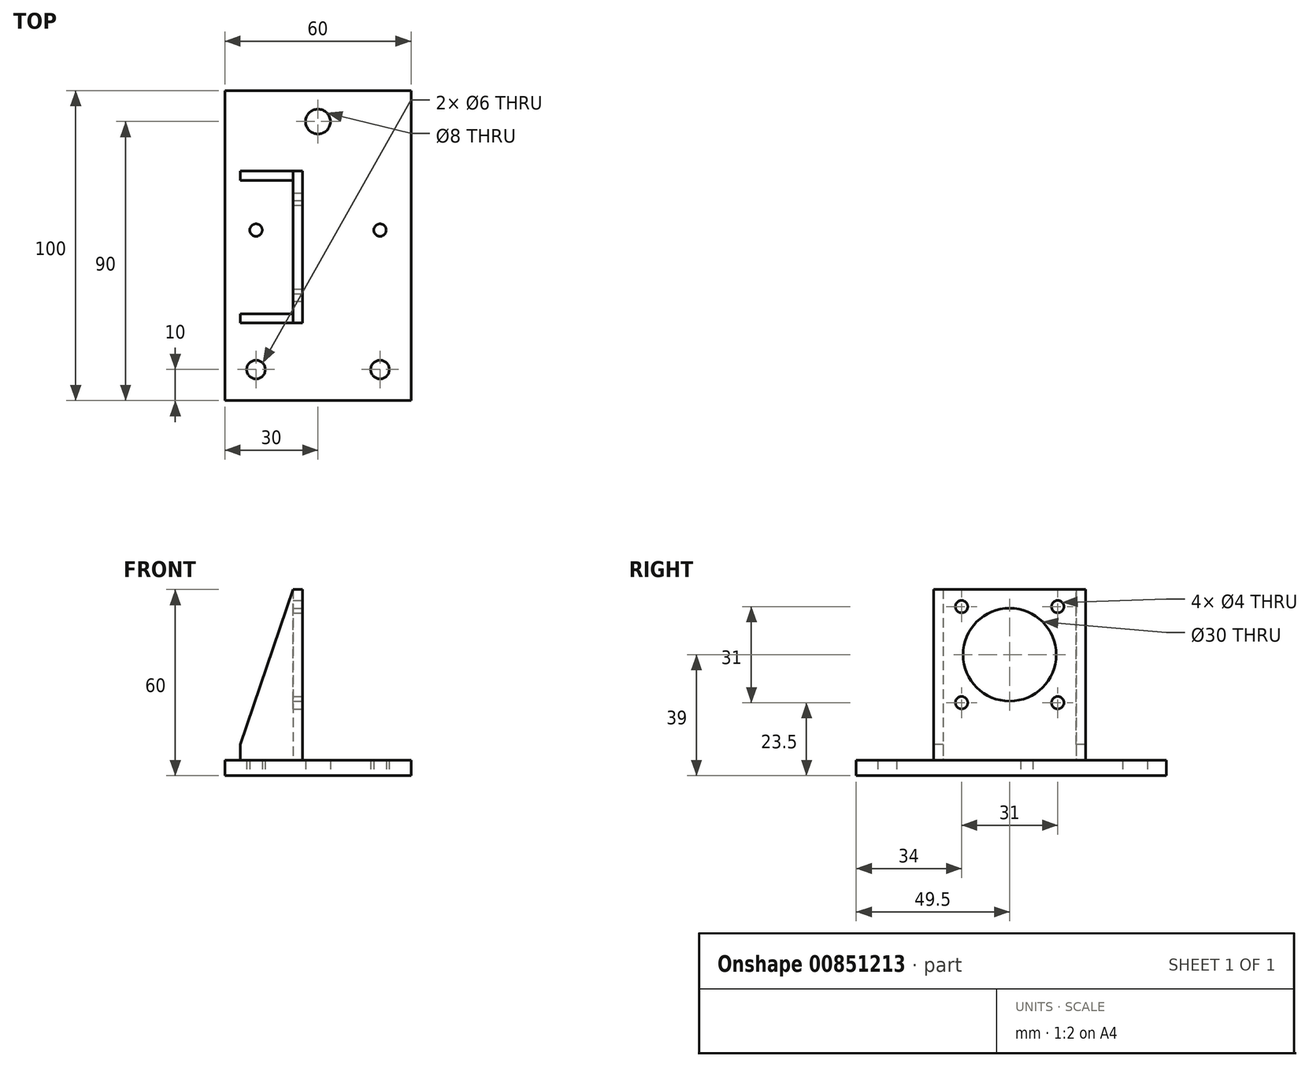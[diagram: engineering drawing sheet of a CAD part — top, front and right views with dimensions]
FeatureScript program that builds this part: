
annotation { "Feature Type Name" : "Feature", "Feature Type Description" : "" }
export const myFeature = defineFeature(function(context is Context, id is Id, definition is map)
    precondition{}
    {
        {
            var Q0;
            Q0=qCreatedBy(makeId("Top.planeOp"),FACE);
            var sketch = newSketch(context, id + "F0", { "sketchPlane" : qUnion([Q0])});
            skLineSegment(sketch, "E0.bottom", {"start": v(0, 0) * mm, "end": v(60, 0) * mm});
            skLineSegment(sketch, "E0.top", {"start": v(0, 100) * mm, "end": v(60, 100) * mm});
            skLineSegment(sketch, "E0.left", {"start": v(0, 0) * mm, "end": v(0, 100) * mm});
            skLineSegment(sketch, "E0.right", {"start": v(60, 0) * mm, "end": v(60, 100) * mm});
            skCircle(sketch, "E1", {"center": v(30, 90) * mm, "radius": 4 * mm});
            skPoint(sketch, "E1.centerSnap0", {"position": v(30, 100) * mm});
            skCircle(sketch, "E2", {"center": v(10, 10) * mm, "radius": 3 * mm});
            skCircle(sketch, "E3", {"center": v(50, 10) * mm, "radius": 3 * mm});
            skCircle(sketch, "E4", {"center": v(10, 55) * mm, "radius": 2 * mm});
            skCircle(sketch, "E5", {"center": v(50, 55) * mm, "radius": 2 * mm});
            skSolve(sketch);
        }
        {
            var Q0;
            Q0 = qSketchRegion(id + "F0", true);
            extrude(context, id + "F1", {"entities" : qUnion([Q0]), "depth" : 5 * mm, "offsetDistance" : 25 * mm});
        }
        {
            var Q0;
            Q0=makeQuery(id+"F1.opExtrude","CAP_FACE",FACE,{"disambiguationData":[OSD([sQuery(id+"F0.wireOp",EDGE,"E0.bottom"),sQuery(id+"F0.wireOp",EDGE,"E0.top"),sQuery(id+"F0.wireOp",EDGE,"E0.left"),sQuery(id+"F0.wireOp",EDGE,"E0.right"),sQuery(id+"F0.wireOp",EDGE,"E1"),sQuery(id+"F0.wireOp",EDGE,"E2"),sQuery(id+"F0.wireOp",EDGE,"E3"),sQuery(id+"F0.wireOp",EDGE,"E4"),sQuery(id+"F0.wireOp",EDGE,"E5")])],"isStart":false});
            var sketch = newSketch(context, id + "F2", { "sketchPlane" : qUnion([Q0])});
            skLineSegment(sketch, "E6", {"start": v(5, 74) * mm, "end": v(5, 71) * mm});
            skLineSegment(sketch, "E7", {"start": v(5, 71) * mm, "end": v(22, 71) * mm});
            skLineSegment(sketch, "E8", {"start": v(22, 71) * mm, "end": v(22, 28) * mm});
            skLineSegment(sketch, "E9", {"start": v(22, 28) * mm, "end": v(5, 28) * mm});
            skLineSegment(sketch, "E10", {"start": v(5, 28) * mm, "end": v(5, 25) * mm});
            skLineSegment(sketch, "E11", {"start": v(5, 25) * mm, "end": v(25, 25) * mm});
            skLineSegment(sketch, "E12", {"start": v(25, 25) * mm, "end": v(25, 74) * mm});
            skLineSegment(sketch, "E13", {"start": v(25, 74) * mm, "end": v(5, 74) * mm});
            skSolve(sketch);
        }
        {
            var Q0;
            Q0 = qSketchRegion(id + "F2", true);
            extrude(context, id + "F3", {"entities" : qUnion([Q0]), "operationType" : NewBodyOperationType.ADD, "depth" : 55 * mm, "offsetDistance" : 25 * mm});
        }
        {
            var Q0;
            Q0=makeQuery(id+"F3.opExtrude","SWEPT_FACE",FACE,{"disambiguationData":[OSD([sQuery(id+"F2.wireOp",EDGE,"E11")])]});
            var sketch = newSketch(context, id + "F4", { "sketchPlane" : qUnion([Q0])});
            skLineSegment(sketch, "E14.0.1", {"start": v(22, 5) * mm, "end": v(22, 60) * mm, "construction": true});
            skLineSegment(sketch, "E14.0.3", {"start": v(22, 60) * mm, "end": v(22, 5) * mm, "construction": true});
            skLineSegment(sketch, "E15.0", {"start": v(5, 60) * mm, "end": v(22, 60) * mm});
            skLineSegment(sketch, "E16.0", {"start": v(5, 60) * mm, "end": v(5, 10) * mm});
            skLineSegment(sketch, "E17", {"start": v(22, 60) * mm, "end": v(5, 10) * mm});
            skPoint(sketch, "E18.orphan", {"position": v(5, 5) * mm});
            skSolve(sketch);
        }
        {
            var Q0;
            Q0 = qSketchRegion(id + "F4", true);
            extrude(context, id + "F5", {"entities" : qUnion([Q0]), "operationType" : NewBodyOperationType.REMOVE, "endBound" : BoundingType.THROUGH_ALL, "oppositeDirection" : true, "depth" : 25 * mm, "offsetDistance" : 25 * mm});
        }
        {
            var Q0;
            Q0=makeQuery(id+"F3.opExtrude","SWEPT_FACE",FACE,{"disambiguationData":[OSD([sQuery(id+"F2.wireOp",EDGE,"E12")])]});
            var sketch = newSketch(context, id + "F6", { "sketchPlane" : qUnion([Q0])});
            skCircle(sketch, "E19", {"center": v(49.5, 39) * mm, "radius": 15 * mm});
            skPoint(sketch, "E19.centerSnap0", {"position": v(49.5, 60) * mm});
            skCircle(sketch, "E20", {"center": v(34, 54.5) * mm, "radius": 2 * mm});
            skCircle(sketch, "E21", {"center": v(65, 54.5) * mm, "radius": 2 * mm});
            skCircle(sketch, "E22", {"center": v(65, 23.5) * mm, "radius": 2 * mm});
            skCircle(sketch, "E23", {"center": v(34, 23.5) * mm, "radius": 2 * mm});
            skSolve(sketch);
        }
        {
            var Q0;
            Q0 = qSketchRegion(id + "F6", true);
            extrude(context, id + "F7", {"entities" : qUnion([Q0]), "operationType" : NewBodyOperationType.REMOVE, "endBound" : BoundingType.THROUGH_ALL, "oppositeDirection" : true, "depth" : 25 * mm, "offsetDistance" : 25 * mm});
        }
    });
